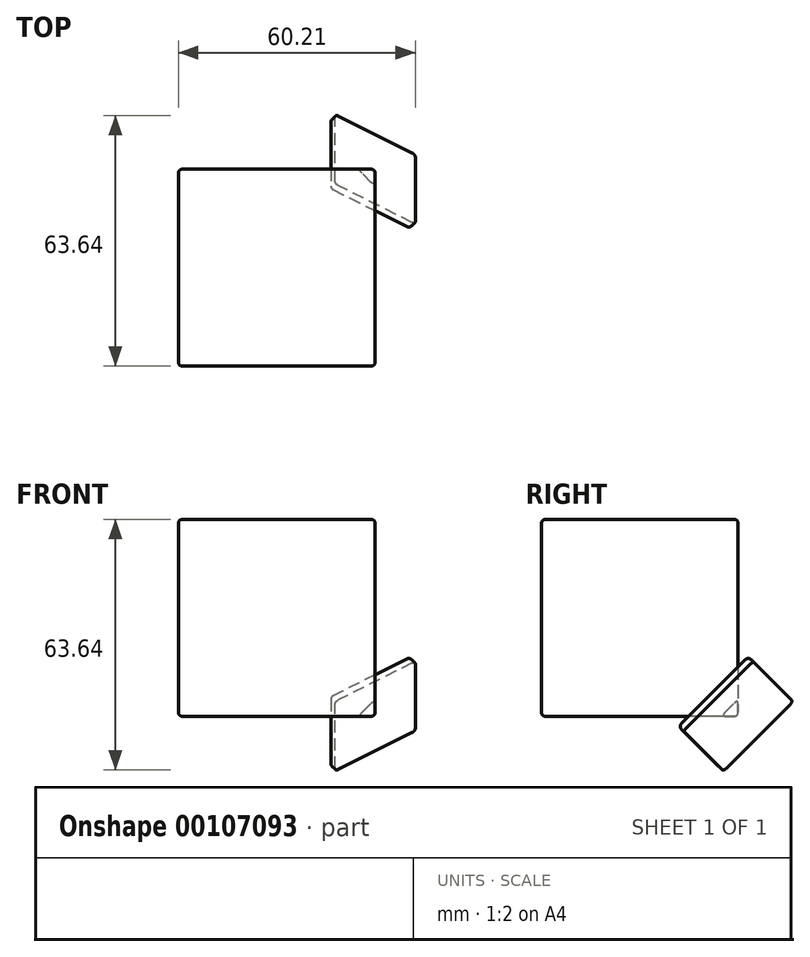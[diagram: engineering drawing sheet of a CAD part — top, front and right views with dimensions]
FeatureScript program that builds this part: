
annotation { "Feature Type Name" : "Feature", "Feature Type Description" : "" }
export const myFeature = defineFeature(function(context is Context, id is Id, definition is map)
    precondition{}
    {
        {
            var Q0;
            Q0=qCreatedBy(makeId("Top.planeOp"),FACE);
            var sketch = newSketch(context, id + "F0", { "sketchPlane" : qUnion([Q0])});
            skLineSegment(sketch, "E0.bottom", {"start": v(25, 25) * mm, "end": v(-25, 25) * mm});
            skLineSegment(sketch, "E0.top", {"start": v(25, -25) * mm, "end": v(-25, -25) * mm});
            skLineSegment(sketch, "E0.left", {"start": v(25, 25) * mm, "end": v(25, -25) * mm});
            skLineSegment(sketch, "E0.right", {"start": v(-25, 25) * mm, "end": v(-25, -25) * mm});
            skPoint(sketch, "E0.middle", {"position": v(0, 0) * mm});
            skSolve(sketch);
        }
        {
            var Q0;
            Q0 = qSketchRegion(id + "F0", true);
            extrude(context, id + "F1", {"entities" : qUnion([Q0]), "endBound" : BoundingType.SYMMETRIC, "depth" : 50 * mm});
        }
        {
            var Q0;
            Q0=makeQuery(id+"F1.opExtrude","CAP_VERTEX",VERTEX,{"disambiguationData":[OSD([sQuery(id+"F0.wireOp",EDGE,"E0.bottom"),sQuery(id+"F0.wireOp",EDGE,"E0.left")])],"isStart":false});
            var Q1;
            Q1=makeQuery(id+"F1.opExtrude","CAP_VERTEX",VERTEX,{"disambiguationData":[OSD([sQuery(id+"F0.wireOp",EDGE,"E0.bottom"),sQuery(id+"F0.wireOp",EDGE,"E0.right")])],"isStart":true});
            var Q2;
            Q2=makeQuery(id+"F1.opExtrude","CAP_VERTEX",VERTEX,{"disambiguationData":[OSD([sQuery(id+"F0.wireOp",EDGE,"E0.top"),sQuery(id+"F0.wireOp",EDGE,"E0.left")])],"isStart":true});
            cPlane(context, id + "F2", {"entities" : qUnion([Q0, Q1, Q2]), "cplaneType" : CPlaneType.THREE_POINT, "offset" : 25 * mm, "width" : 150 * mm, "height" : 150 * mm});
        }
        {
            var Q0;
            Q0=qCreatedBy(id+"F2.planeOp",FACE);
            var Q1;
            Q1=makeQuery(id+"F1.opExtrude","CAP_VERTEX",VERTEX,{"disambiguationData":[OSD([sQuery(id+"F0.wireOp",EDGE,"E0.bottom"),sQuery(id+"F0.wireOp",EDGE,"E0.left")])],"isStart":true});
            cPlane(context, id + "F3", {"entities" : qUnion([Q0, Q1]), "cplaneType" : CPlaneType.PLANE_POINT, "offset" : 25 * mm, "width" : 150 * mm, "height" : 150 * mm});
        }
        {
            var Q0;
            Q0=qCreatedBy(id+"F3.planeOp",FACE);
            var sketch = newSketch(context, id + "F4", { "sketchPlane" : qUnion([Q0])});
            skLineSegment(sketch, "E1.bottom", {"start": v(-12.5, -12.5) * mm, "end": v(12.5, -12.5) * mm});
            skLineSegment(sketch, "E1.top", {"start": v(-12.5, 12.5) * mm, "end": v(12.5, 12.5) * mm});
            skLineSegment(sketch, "E1.left", {"start": v(-12.5, -12.5) * mm, "end": v(-12.5, 12.5) * mm});
            skLineSegment(sketch, "E1.right", {"start": v(12.5, -12.5) * mm, "end": v(12.5, 12.5) * mm});
            skPoint(sketch, "E1.middle", {"position": v(0, 0) * mm});
            skSolve(sketch);
        }
        {
            var Q0;
            Q0 = qSketchRegion(id + "F4", true);
            extrude(context, id + "F5", {"entities" : qUnion([Q0]), "operationType" : NewBodyOperationType.ADD, "oppositeDirection" : true, "depth" : 2.5 * mm});
        }
        {
            var Q0;
            Q0=makeQuery(id+"F1.opExtrude","CAP_FACE",FACE,{"disambiguationData":[OSD([sQuery(id+"F0.wireOp",EDGE,"E0.bottom"),sQuery(id+"F0.wireOp",EDGE,"E0.top"),sQuery(id+"F0.wireOp",EDGE,"E0.left"),sQuery(id+"F0.wireOp",EDGE,"E0.right")])],"isStart":false});
            var Q1;
            Q1=makeQuery(id+"F1.opExtrude","SWEPT_FACE",FACE,{"disambiguationData":[OSD([sQuery(id+"F0.wireOp",EDGE,"E0.right")])]});
            var Q2;
            Q2=makeQuery(id+"F1.opExtrude","SWEPT_FACE",FACE,{"disambiguationData":[OSD([sQuery(id+"F0.wireOp",EDGE,"E0.top")])]});
            var Q3;
            Q3=makeQuery(id+"F1.opExtrude","CAP_EDGE",EDGE,{"disambiguationData":[OSD([sQuery(id+"F0.wireOp",EDGE,"E0.bottom")])],"isStart":true});
            var Q4;
            Q4=makeQuery(id+"F1.opExtrude","CAP_EDGE",EDGE,{"disambiguationData":[OSD([sQuery(id+"F0.wireOp",EDGE,"E0.left")])],"isStart":true});
            var Q5;
            Q5=makeQuery(id+"F1.opExtrude","SWEPT_EDGE",EDGE,{"disambiguationData":[OSD([sQuery(id+"F0.wireOp",EDGE,"E0.bottom"),sQuery(id+"F0.wireOp",EDGE,"E0.left")])]});
            var Q6;
            Q6=makeQuery(id+"F5.opExtrude","CAP_EDGE",EDGE,{"disambiguationData":[OSD([sQuery(id+"F4.wireOp",EDGE,"E1.left")])],"isStart":false});
            var Q7;
            Q7=makeQuery(id+"F5.opExtrude","CAP_EDGE",EDGE,{"disambiguationData":[OSD([sQuery(id+"F4.wireOp",EDGE,"E1.bottom")])],"isStart":false});
            var Q8;
            Q8=makeQuery(id+"F5.opExtrude","CAP_EDGE",EDGE,{"disambiguationData":[OSD([sQuery(id+"F4.wireOp",EDGE,"E1.right")])],"isStart":false});
            var Q9;
            Q9=makeQuery(id+"F5.opExtrude","CAP_EDGE",EDGE,{"disambiguationData":[OSD([sQuery(id+"F4.wireOp",EDGE,"E1.top")])],"isStart":false});
            var Q10;
            Q10=makeQuery(id+"F5.opExtrude","SWEPT_EDGE",EDGE,{"disambiguationData":[OSD([sQuery(id+"F4.wireOp",EDGE,"E1.top"),sQuery(id+"F4.wireOp",EDGE,"E1.left")])]});
            var Q11;
            Q11=makeQuery(id+"F5.opExtrude","SWEPT_EDGE",EDGE,{"disambiguationData":[OSD([sQuery(id+"F4.wireOp",EDGE,"E1.top"),sQuery(id+"F4.wireOp",EDGE,"E1.right")])]});
            var Q12;
            Q12=makeQuery(id+"F5.opExtrude","SWEPT_EDGE",EDGE,{"disambiguationData":[OSD([sQuery(id+"F4.wireOp",EDGE,"E1.bottom"),sQuery(id+"F4.wireOp",EDGE,"E1.left")])]});
            var Q13;
            Q13=makeQuery(id+"F5.opExtrude","SWEPT_EDGE",EDGE,{"disambiguationData":[OSD([sQuery(id+"F4.wireOp",EDGE,"E1.bottom"),sQuery(id+"F4.wireOp",EDGE,"E1.right")])]});
            fillet(context, id + "F6", {"entities" : qUnion([Q0, Q1, Q2, Q3, Q4, Q5, Q6, Q7, Q8, Q9, Q10, Q11, Q12, Q13]), "radius" : 1 * mm, "tangentPropagation" : true, "allowEdgeOverflow" : false});
        }
    });
